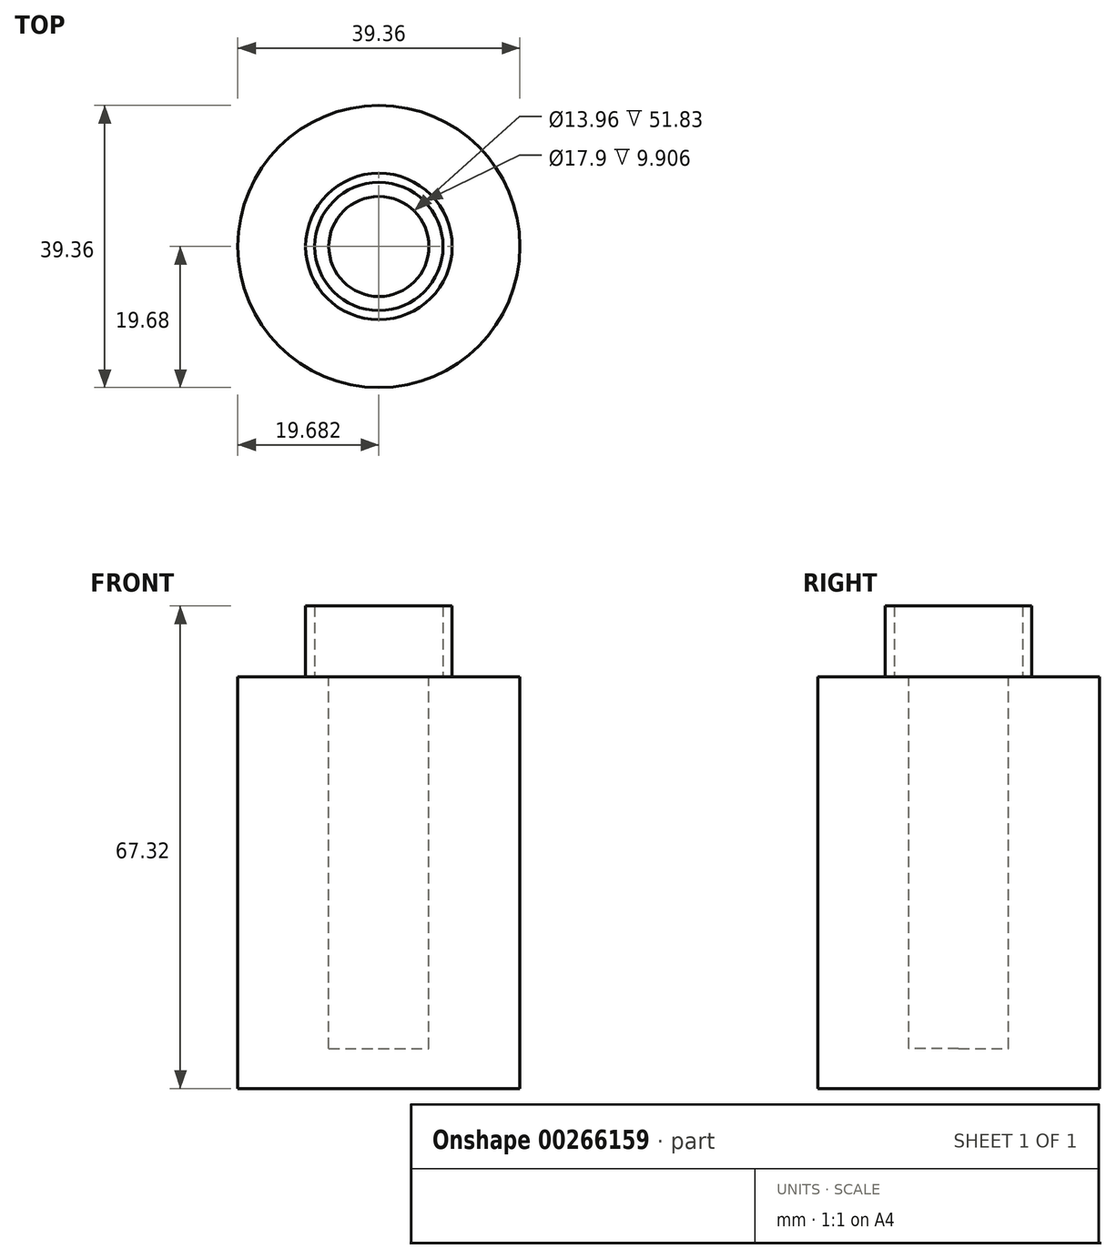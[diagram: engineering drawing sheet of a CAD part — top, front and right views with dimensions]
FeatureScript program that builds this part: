
annotation { "Feature Type Name" : "Feature", "Feature Type Description" : "" }
export const myFeature = defineFeature(function(context is Context, id is Id, definition is map)
    precondition{}
    {
        {
            var Q0;
            Q0=qCreatedBy(makeId("Front.planeOp"),FACE);
            var sketch = newSketch(context, id + "F0", { "sketchPlane" : qUnion([Q0])});
            skLineSegment(sketch, "E0", {"start": v(14.5, 30.52) * mm, "end": v(14.5, -14.83) * mm});
            skLineSegment(sketch, "E1.bottom", {"start": v(21.48, 35.35) * mm, "end": v(34.18, 35.35) * mm});
            skLineSegment(sketch, "E1.top", {"start": v(21.48, -22.07) * mm, "end": v(34.18, -22.07) * mm});
            skLineSegment(sketch, "E1.left", {"start": v(21.48, 35.35) * mm, "end": v(21.48, -22.07) * mm});
            skLineSegment(sketch, "E1.right", {"start": v(34.18, 35.35) * mm, "end": v(34.18, -22.07) * mm});
            skSolve(sketch);
        }
        {
            var Q0;
            Q0=makeQuery(id+"F0.imprint","IMPRINT",FACE,{"disambiguationData":[TD([[makeQuery(id+"F0.imprint","IMPRINT",EDGE,{"derivedFrom":sQuery(id+"F0.wireOp",EDGE,"E1.bottom")}),-1.0]])]});
            var Q1;
            Q1=sQuery(id+"F0.wireOp",EDGE,"E0");
            revolve(context, id + "F1", {"entities" : qUnion([Q0]), "axis" : qUnion([Q1]), "revolveType" : RevolveType.FULL});
        }
        {
            var Q0;
            Q0=makeQuery(id+"F1.opRevolve","SWEPT_FACE",FACE,{"disambiguationData":[OSD([sQuery(id+"F0.wireOp",EDGE,"E1.top")])]});
            var sketch = newSketch(context, id + "F2", { "sketchPlane" : qUnion([Q0])});
            skSolve(sketch);
        }
        {
            var Q0;
            Q0=makeQuery(id+"F2.imprint","IMPRINT",FACE,{"disambiguationData":[TD([[makeQuery(id+"F2.imprint","IMPRINT",EDGE,{"derivedFrom":makeQuery(id+"F1.opRevolve","SWEPT_EDGE",EDGE,{"disambiguationData":[OSD([sQuery(id+"F0.wireOp",EDGE,"E1.top"),sQuery(id+"F0.wireOp",EDGE,"E1.left")])]})}),-1.0]])]});
            extrude(context, id + "F3", {"entities" : qUnion([Q0]), "operationType" : NewBodyOperationType.ADD, "oppositeDirection" : true, "depth" : 5.6 * mm});
        }
        {
            var Q0;
            Q0=makeQuery(id+"F1.opRevolve","SWEPT_FACE",FACE,{"disambiguationData":[OSD([sQuery(id+"F0.wireOp",EDGE,"E1.bottom")])]});
            var sketch = newSketch(context, id + "F4", { "sketchPlane" : qUnion([Q0])});
            skCircle(sketch, "E2", {"center": v(14.5, 0) * mm, "radius": 10.22 * mm});
            skCircle(sketch, "E3", {"center": v(14.5, 0) * mm, "radius": 8.95 * mm});
            skSolve(sketch);
        }
        {
            var Q0;
            Q0 = qSketchRegion(id + "F4", true);
            extrude(context, id + "F5", {"entities" : qUnion([Q0]), "operationType" : NewBodyOperationType.ADD, "depth" : 9.9 * mm});
        }
    });
